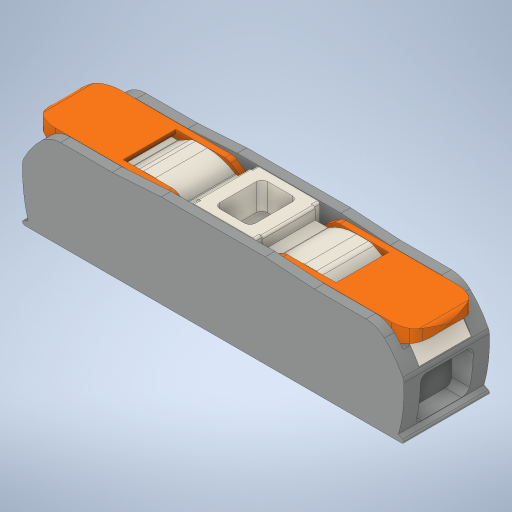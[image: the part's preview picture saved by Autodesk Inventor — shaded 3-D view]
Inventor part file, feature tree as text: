
AUTODESK INVENTOR PART (.ipt)
format: ipt  version: 2024 (Build 280153000, 153)  size: 606,208 bytes
history: native  units: mm
features: extrude x17, sketch x17
ambient origin geometry x8: Origin, YZ Plane, XZ Plane, XY Plane, X Axis, Y Axis, Z Axis, Center Point
bodies: Solid1 (feature_tree)
feature tree (34):
  extrude  "Extrusion1"  Depth=7.9mm TaperAngle=0.0deg
  extrude  "Extrusion2"  Depth=4.82mm TaperAngle=0.0deg
  extrude  "Extrusion3"  Depth=0.6mm TaperAngle=0.0deg
  extrude  "Extrusion4"  Depth=0.6mm TaperAngle=0.0deg
  extrude  "Extrusion5"  Depth=0.6mm TaperAngle=0.0deg
  extrude  "Extrusion6"  Depth=1.6mm TaperAngle=0.0deg
  extrude  "Extrusion7"  Depth=5.0mm TaperAngle=0.0deg
  extrude  "Extrusion8"  Depth=2.0mm TaperAngle=0.0deg
  extrude  "Extrusion9"  [1 undecoded]
  extrude  "Extrusion10"  [1 undecoded]
  extrude  "Extrusion11"  [1 undecoded]
  extrude  "Extrusion12"  [1 undecoded]
  extrude  "Extrusion13"  [1 undecoded]
  extrude  "Extrusion14"  [1 undecoded]
  extrude  "Extrusion15"  [1 undecoded]
  extrude  "Extrusion16"  [1 undecoded]
  extrude  "Extrusion17"  [1 undecoded]
  sketch  "Sketch_1"  dims[d0=7.9mm d1=0.0mm d2=6.1mm d3=0.0mm]
  sketch  "Sketch_2"  dims[d4=4.83mm d5=0.0mm d6=4.82mm d7=0.0mm]
  sketch  "Sketch_3"  dims[d8=6.0mm d9=0.0mm d10=0.6mm d11=0.0mm]
  sketch  "Sketch_4"  dims[d12=0.6mm d13=0.0mm d14=0.6mm d15=0.0mm]
  sketch  "Sketch_5"  dims[d16=0.6mm d17=0.0mm d18=4.86mm d19=0.0mm]
  sketch  "Sketch_6"  dims[d20=4.86mm d21=0.0mm d22=1.6mm d23=0.0mm]
  sketch  "Sketch_7"  dims[d24=1.6mm d25=0.0mm d26=5.0mm d27=0.0mm]
  sketch  "Sketch_8"  dims[d28=2.0mm d29=0.0mm d30=2.0mm d31=0.0mm]
  sketch  "Sketch_9"  dims[d32=7.9mm d33=0.0mm]
  sketch  "Sketch_10"
  sketch  "Sketch_11"
  sketch  "Sketch_12"
  sketch  "Sketch_13"
  sketch  "Sketch_14"
  sketch  "Sketch_15"
  sketch  "Sketch_16"
  sketch  "Sketch_17"
note: 9 required parameter values undecoded (feature->parameter linkage not recoverable at this tier; creation-order binding heuristic only, values carry confidence <= 0.55)
